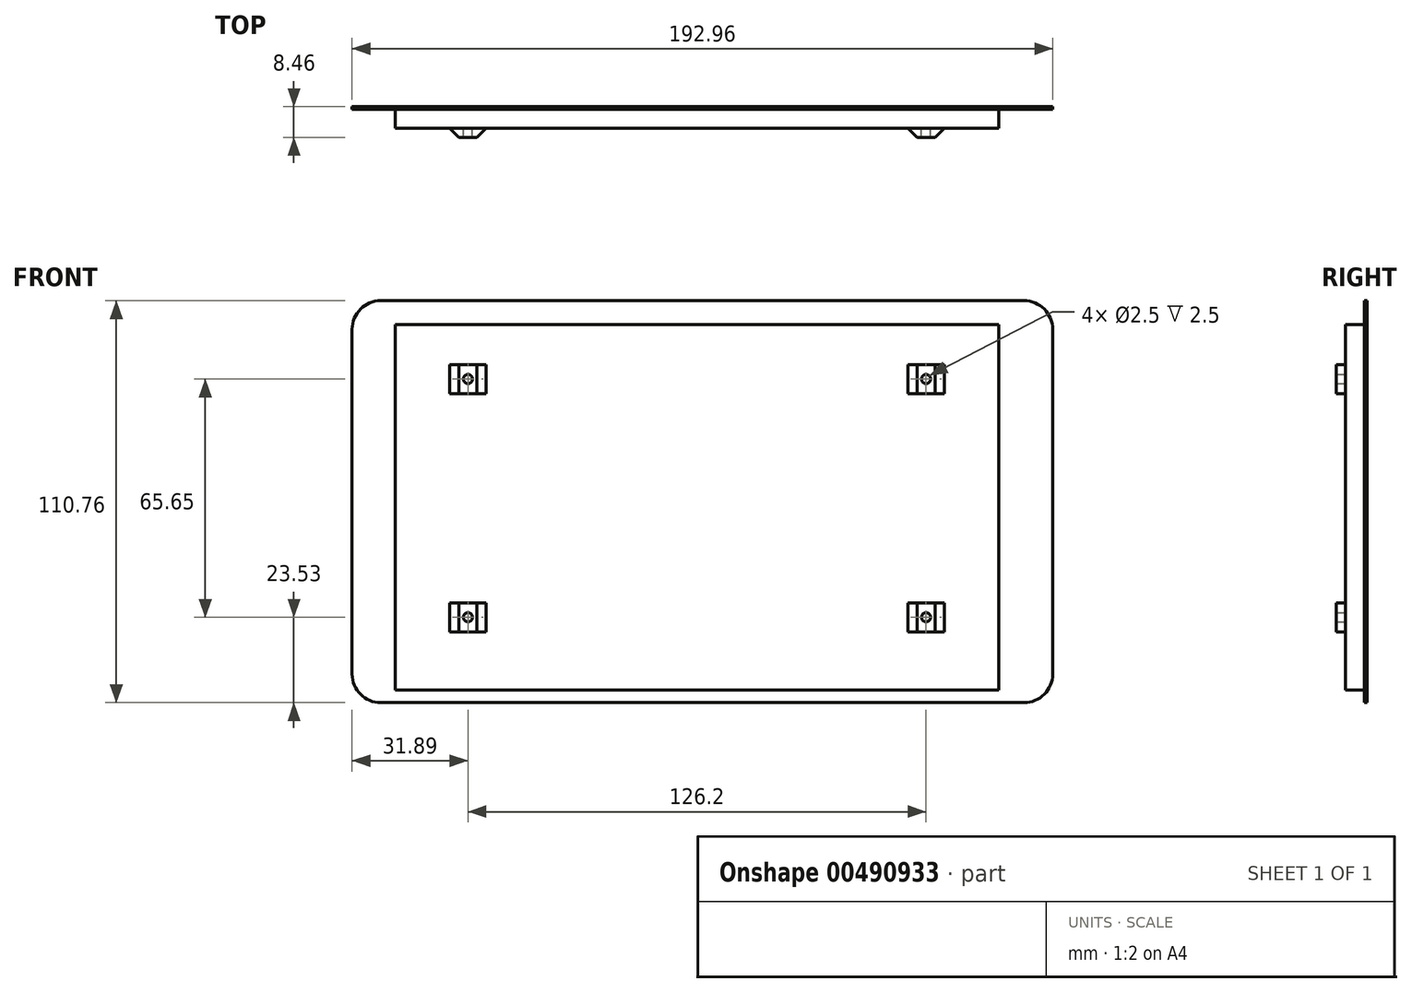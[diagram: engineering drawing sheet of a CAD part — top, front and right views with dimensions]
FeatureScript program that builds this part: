
annotation { "Feature Type Name" : "Feature", "Feature Type Description" : "" }
export const myFeature = defineFeature(function(context is Context, id is Id, definition is map)
    precondition{}
    {
        {
            var Q0;
            Q0=qCreatedBy(makeId("Front.planeOp"),FACE);
            var sketch = newSketch(context, id + "F0", { "sketchPlane" : qUnion([Q0])});
            skLineSegment(sketch, "E0.bottom", {"start": v(-88.6, -55.38) * mm, "end": v(88.6, -55.38) * mm});
            skLineSegment(sketch, "E0.top", {"start": v(-88.6, 55.38) * mm, "end": v(88.6, 55.38) * mm});
            skLineSegment(sketch, "E0.left", {"start": v(-96.48, -47.5) * mm, "end": v(-96.48, 47.5) * mm});
            skLineSegment(sketch, "E0.right", {"start": v(96.48, -47.5) * mm, "end": v(96.48, 47.5) * mm});
            skPoint(sketch, "E0.middle", {"position": v(0, 0) * mm});
            skLineSegment(sketch, "E1.bottom", {"start": v(81.6, -51.85) * mm, "end": v(-84.6, -51.85) * mm});
            skLineSegment(sketch, "E1.top", {"start": v(81.6, 48.75) * mm, "end": v(-84.6, 48.75) * mm});
            skLineSegment(sketch, "E1.left", {"start": v(81.6, -51.85) * mm, "end": v(81.6, 48.75) * mm});
            skLineSegment(sketch, "E1.right", {"start": v(-84.6, -51.85) * mm, "end": v(-84.6, 48.75) * mm});
            skPoint(sketch, "E1.middle", {"position": v(-1.5, -1.55) * mm});
            skPoint(sketch, "E2.visualSharp", {"position": v(-96.48, 55.38) * mm});
            skArc(sketch, "E2.filletArc", {"start": v(-88.6, 55.38) * mm, "mid": v(-94.17, 53.07) * mm, "end": v(-96.48, 47.5) * mm});
            skPoint(sketch, "E3.visualSharp", {"position": v(-96.48, -55.38) * mm});
            skArc(sketch, "E3.filletArc", {"start": v(-96.48, -47.5) * mm, "mid": v(-94.17, -53.07) * mm, "end": v(-88.6, -55.38) * mm});
            skPoint(sketch, "E4.visualSharp", {"position": v(96.48, -55.38) * mm});
            skArc(sketch, "E4.filletArc", {"start": v(88.6, -55.38) * mm, "mid": v(94.17, -53.07) * mm, "end": v(96.48, -47.5) * mm});
            skPoint(sketch, "E5.visualSharp", {"position": v(96.48, 55.38) * mm});
            skArc(sketch, "E5.filletArc", {"start": v(96.48, 47.5) * mm, "mid": v(94.17, 53.07) * mm, "end": v(88.6, 55.38) * mm});
            skSolve(sketch);
        }
        {
            var Q0;
            Q0=makeQuery(id+"F0.imprint","IMPRINT",FACE,{"disambiguationData":[TD([[makeQuery(id+"F0.imprint","IMPRINT",EDGE,{"derivedFrom":sQuery(id+"F0.wireOp",EDGE,"E1.bottom")}),-1.0]])]});
            extrude(context, id + "F1", {"entities" : qUnion([Q0]), "depth" : 5.96 * mm});
        }
        {
            var Q0;
            Q0 = qSketchRegion(id + "F0", true);
            extrude(context, id + "F2", {"entities" : qUnion([Q0]), "operationType" : NewBodyOperationType.ADD, "depth" : 0.7 * mm});
        }
        {
            var Q0;
            Q0=makeQuery(id+"F1.opExtrude","CAP_FACE",FACE,{"disambiguationData":[OSD([sQuery(id+"F0.wireOp",EDGE,"E1.bottom"),sQuery(id+"F0.wireOp",EDGE,"E1.top"),sQuery(id+"F0.wireOp",EDGE,"E1.left"),sQuery(id+"F0.wireOp",EDGE,"E1.right")])],"isStart":false});
            var sketch = newSketch(context, id + "F3", { "sketchPlane" : qUnion([Q0])});
            skLineSegment(sketch, "E6.bottom", {"start": v(-57.1, 29.8) * mm, "end": v(-72.1, 29.8) * mm});
            skLineSegment(sketch, "E6.top", {"start": v(-57.1, 37.8) * mm, "end": v(-72.1, 37.8) * mm});
            skLineSegment(sketch, "E6.left", {"start": v(-57.1, 29.8) * mm, "end": v(-57.1, 37.8) * mm});
            skLineSegment(sketch, "E6.right", {"start": v(-72.1, 29.8) * mm, "end": v(-72.1, 37.8) * mm});
            skPoint(sketch, "E6.middle", {"position": v(-64.6, 33.8) * mm});
            skLineSegment(sketch, "E7.bottom", {"start": v(-64.6, 33.8) * mm, "end": v(61.61, 33.8) * mm, "construction": true});
            skLineSegment(sketch, "E7.top", {"start": v(-64.6, -31.85) * mm, "end": v(61.6, -31.85) * mm, "construction": true});
            skLineSegment(sketch, "E7.left", {"start": v(-64.6, 33.8) * mm, "end": v(-64.6, -31.85) * mm, "construction": true});
            skLineSegment(sketch, "E7.right", {"start": v(61.6, 33.8) * mm, "end": v(61.6, -31.85) * mm, "construction": true});
            skPoint(sketch, "E7.middle", {"position": v(-1.5, 0.98) * mm});
            skLineSegment(sketch, "E8.bottom", {"start": v(-72.1, -35.85) * mm, "end": v(-57.1, -35.85) * mm});
            skLineSegment(sketch, "E8.top", {"start": v(-72.1, -27.85) * mm, "end": v(-57.1, -27.85) * mm});
            skLineSegment(sketch, "E8.left", {"start": v(-72.1, -35.85) * mm, "end": v(-72.1, -27.85) * mm});
            skLineSegment(sketch, "E8.right", {"start": v(-57.1, -35.85) * mm, "end": v(-57.1, -27.85) * mm});
            skPoint(sketch, "E8.middle", {"position": v(-64.6, -31.85) * mm});
            skLineSegment(sketch, "E9.bottom", {"start": v(69.11, -35.85) * mm, "end": v(54.1, -35.85) * mm});
            skLineSegment(sketch, "E9.top", {"start": v(69.11, -27.85) * mm, "end": v(54.1, -27.85) * mm});
            skLineSegment(sketch, "E9.left", {"start": v(69.11, -35.85) * mm, "end": v(69.11, -27.85) * mm});
            skLineSegment(sketch, "E9.right", {"start": v(54.1, -35.85) * mm, "end": v(54.1, -27.85) * mm});
            skPoint(sketch, "E9.middle", {"position": v(61.6, -31.85) * mm});
            skLineSegment(sketch, "E10.bottom", {"start": v(69.11, 29.8) * mm, "end": v(54.11, 29.8) * mm});
            skLineSegment(sketch, "E10.top", {"start": v(69.11, 37.8) * mm, "end": v(54.11, 37.8) * mm});
            skLineSegment(sketch, "E10.left", {"start": v(69.11, 29.8) * mm, "end": v(69.11, 37.8) * mm});
            skLineSegment(sketch, "E10.right", {"start": v(54.11, 29.8) * mm, "end": v(54.11, 37.8) * mm});
            skPoint(sketch, "E10.middle", {"position": v(61.61, 33.8) * mm});
            skSolve(sketch);
        }
        {
            var Q0;
            Q0 = qSketchRegion(id + "F3", true);
            extrude(context, id + "F4", {"entities" : qUnion([Q0]), "operationType" : NewBodyOperationType.ADD, "depth" : 2.5 * mm});
        }
        {
            var Q0;
            Q0=makeQuery(id+"F4.opExtrude","CAP_EDGE",EDGE,{"disambiguationData":[OSD([sQuery(id+"F3.wireOp",EDGE,"E6.right")])],"isStart":false});
            var Q1;
            Q1=makeQuery(id+"F4.opExtrude","CAP_EDGE",EDGE,{"disambiguationData":[OSD([sQuery(id+"F3.wireOp",EDGE,"E6.left")])],"isStart":false});
            var Q2;
            Q2=makeQuery(id+"F4.opExtrude","CAP_EDGE",EDGE,{"disambiguationData":[OSD([sQuery(id+"F3.wireOp",EDGE,"E8.left")])],"isStart":false});
            var Q3;
            Q3=makeQuery(id+"F4.opExtrude","CAP_EDGE",EDGE,{"disambiguationData":[OSD([sQuery(id+"F3.wireOp",EDGE,"E8.right")])],"isStart":false});
            var Q4;
            Q4=makeQuery(id+"F4.opExtrude","CAP_EDGE",EDGE,{"disambiguationData":[OSD([sQuery(id+"F3.wireOp",EDGE,"E10.right")])],"isStart":false});
            var Q5;
            Q5=makeQuery(id+"F4.opExtrude","CAP_EDGE",EDGE,{"disambiguationData":[OSD([sQuery(id+"F3.wireOp",EDGE,"E10.left")])],"isStart":false});
            var Q6;
            Q6=makeQuery(id+"F4.opExtrude","CAP_EDGE",EDGE,{"disambiguationData":[OSD([sQuery(id+"F3.wireOp",EDGE,"E9.right")])],"isStart":false});
            var Q7;
            Q7=makeQuery(id+"F4.opExtrude","CAP_EDGE",EDGE,{"disambiguationData":[OSD([sQuery(id+"F3.wireOp",EDGE,"E9.left")])],"isStart":false});
            chamfer(context, id + "F5", {"entities" : qUnion([Q0, Q1, Q2, Q3, Q4, Q5, Q6, Q7]), "width" : 5 * mm, "tangentPropagation" : true});
        }
        {
            var Q0;
            Q0=sQuery(id+"F3.wireOp",VERTEX,"E6.middle");
            var Q1;
            Q1=sQuery(id+"F3.wireOp",VERTEX,"E8.middle");
            var Q2;
            Q2=sQuery(id+"F3.wireOp",VERTEX,"E9.middle");
            var Q3;
            Q3=sQuery(id+"F3.wireOp",VERTEX,"E10.middle");
            var Q4;
            Q4=makeQuery(id+"F1.opExtrude","SWEPT_BODY",BODY,{"disambiguationData":[OSD([sQuery(id+"F0.wireOp",EDGE,"E1.bottom"),sQuery(id+"F0.wireOp",EDGE,"E1.top"),sQuery(id+"F0.wireOp",EDGE,"E1.left"),sQuery(id+"F0.wireOp",EDGE,"E1.right")])]});
            hole(context, id + "F6", {"style" : HoleStyle.SIMPLE, "endStyle" : HoleEndStyle.THROUGH, "oppositeDirection" : true, "standardTappedOrClearance" : lookupTablePath({ "standard" : "ISO", "engagement" : "75%", "pitch" : "0.5 mm", "size" : "M3", "type" : "Tapped" }), "standardBlindInLast" : lookupTablePath({ "standard" : "ISO", "engagement" : "75%", "pitch" : "0.5 mm", "size" : "M3", "type" : "Tapped" }), "holeDiameter" : 2.5 * mm, "showTappedDepth" : true, "isTappedThrough" : true, "tappedDepth" : 0.5 * mm, "tapClearance" : 3, "locations" : qUnion([Q0, Q1, Q2, Q3]), "scope" : qUnion([Q4]), "majorDiameter" : 3 * mm});
        }
    });
